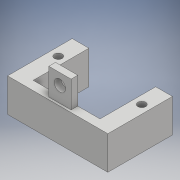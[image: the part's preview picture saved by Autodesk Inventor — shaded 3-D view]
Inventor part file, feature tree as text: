
AUTODESK INVENTOR PART (.ipt)
format: ipt  version: 2018 (Build 220112000, 112)  size: 272,896 bytes
history: native  units: mm
features: extrude x6, sketch x6
ambient origin geometry x8: Origin, YZ Plane, XZ Plane, XY Plane, X Axis, Y Axis, Z Axis, Center Point
bodies: Solid1 (feature_tree)
feature tree (12):
  extrude  "Extrusion1"  Depth=27.0mm
  extrude  "Extrusion2"  Depth=10.0mm
  extrude  "Extrusion4"  Depth=10.0mm TaperAngle=0.0deg
  extrude  "Extrusion5"  Depth=27.0mm TaperAngle=0.0deg
  extrude  "Extrusion6"  Depth=15.0mm
  extrude  "Extrusion7"  Depth=4.0mm TaperAngle=0.0deg
  sketch  "Sketch1"  dims[d0=10.0mm d1=27.0mm]
  sketch  "Sketch2"  dims[d2=10.0mm d3=0.0mm d4=5.0mm]
  sketch  "Sketch4"  dims[d5=5.1mm d6=10.0mm d7=0.0mm]
  sketch  "Sketch5"  dims[d13=27.0mm d14=7.0mm d15=0.0mm]
  sketch  "Sketch6"  dims[d16=22.5mm d17=15.0mm]
  sketch  "Sketch7"  dims[d18=22.5mm d19=4.0mm d20=0.0mm d21=15.0mm d22=15.0mm d23=25.0mm d24=0.0mm d25=15.0mm d26=15.0mm d27=3.5mm d28=3.5mm d29=25.0mm d30=0.0mm]
